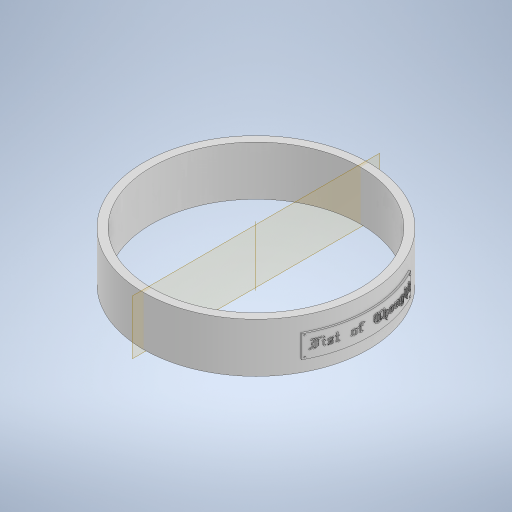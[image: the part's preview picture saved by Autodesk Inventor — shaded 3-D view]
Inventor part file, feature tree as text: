
AUTODESK INVENTOR PART (.ipt)
format: ipt  version: 2023 (Build 270158000, 158)  size: 5,699,584 bytes
history: native  units: in
note: dims shown in document units (in); Inventor stores cm internally (conversion verified against a paired STEP export)
features: emboss x3, pattern_circular x3, other x2, extrude x1, plane x1, fillet x1, sketch x1
ambient origin geometry x8: Origin, YZ Plane, XZ Plane, XY Plane, X Axis, Y Axis, Z Axis, Center Point
bodies: Solid1 (feature_tree)
feature tree (12):
  extrude  "Extrusion1"  Depth=1.9685in
  plane  "Work Plane1"
  other  "Text"
  emboss  "Emboss4"
  emboss  "Emboss5"
  emboss  "Emboss6"
  fillet  "Rivots"  Radius=0.8661in
  pattern_circular  "Circular Pattern1"  Count=6  [1 undecoded]
  pattern_circular  "Circular Pattern2"  [2 undecoded]
  pattern_circular  "Circular Pattern3"  [2 undecoded]
  sketch  "Sketch1"  dims[d0=3.937in d1=3.6614in d2=0.8661in d3=0.0in d4=2.3622in d6=0.4546in d10=0.0in d11=0.3937in d12=1.9685in d19=0.0in d20=0.0in d21=0.0295in d22=0.0in d23=0.0197in d24=0.0in d25=0.0295in d26=0.0295in d27=0.0295in d28=0.0157in d29=0.0in d30=0.0138in d31=0.7874in d32=360.0deg d34=0.7874in d35=360.0deg d37=0.7874in d38=360.0deg d33=0.0in]
  other  "NamePlate"
note: 5 required parameter values undecoded (feature->parameter linkage not recoverable at this tier; creation-order binding heuristic only, values carry confidence <= 0.55)
